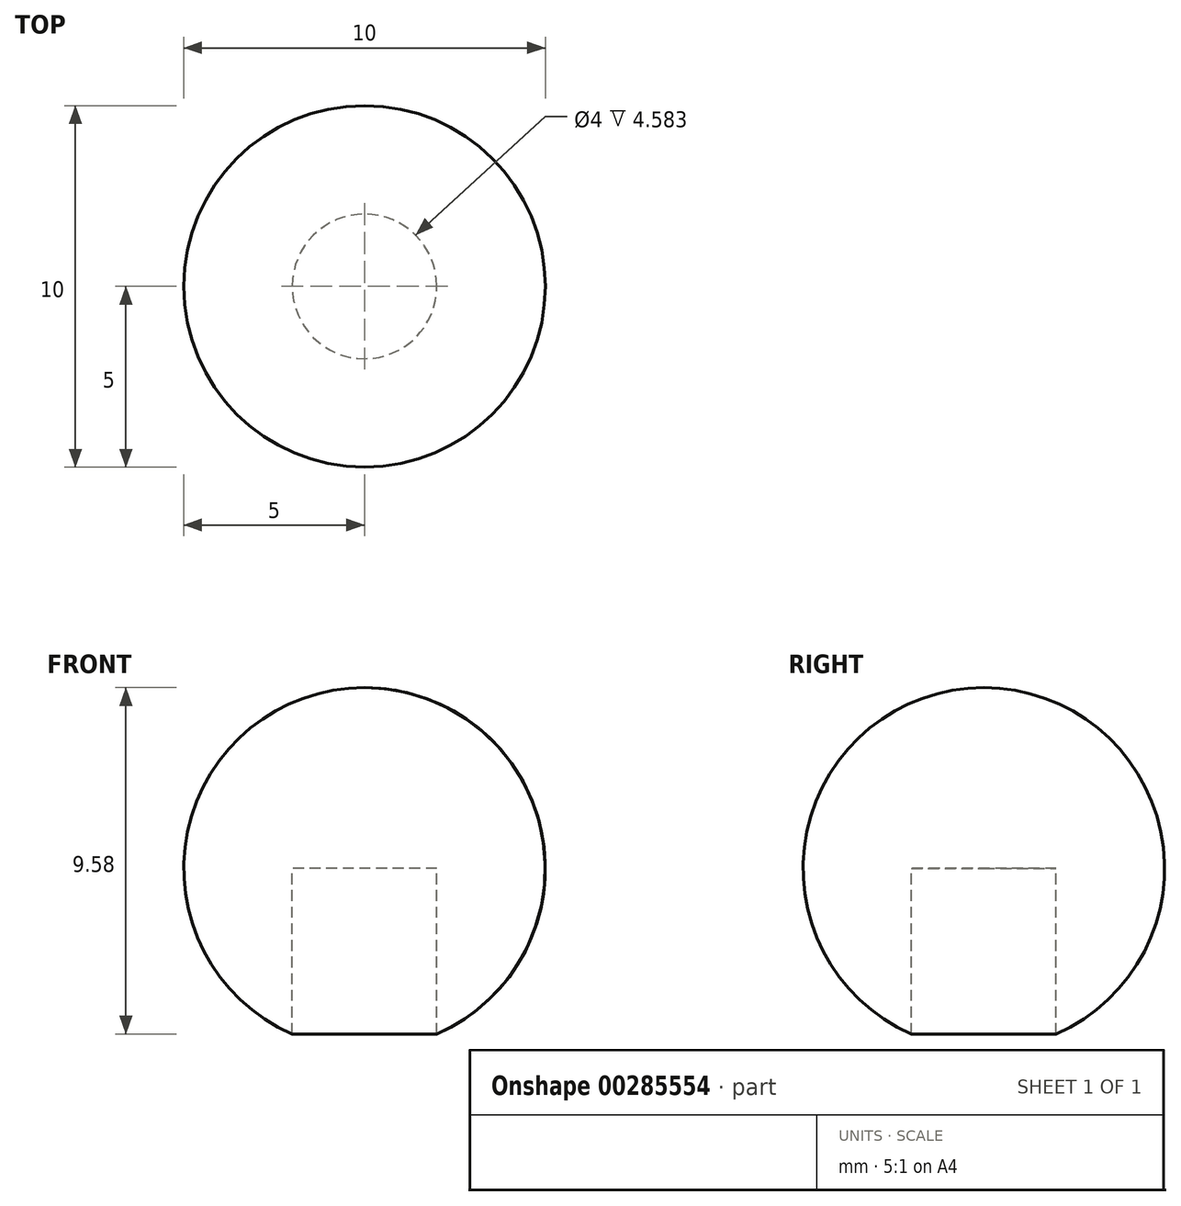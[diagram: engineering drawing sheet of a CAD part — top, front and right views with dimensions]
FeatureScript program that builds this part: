
annotation { "Feature Type Name" : "Feature", "Feature Type Description" : "" }
export const myFeature = defineFeature(function(context is Context, id is Id, definition is map)
    precondition{}
    {
        {
            var Q0;
            Q0=qCreatedBy(makeId("Front.planeOp"),FACE);
            var sketch = newSketch(context, id + "F0", { "sketchPlane" : qUnion([Q0])});
            skArc(sketch, "E0", {"start": v(0, 5) * mm, "mid": v(-5, 0) * mm, "end": v(0, -5) * mm});
            skLineSegment(sketch, "E1", {"start": v(0, 5) * mm, "end": v(0, -5) * mm});
            skSolve(sketch);
        }
        {
            var Q0;
            Q0=makeQuery(id+"F0.imprint","IMPRINT",FACE,{"disambiguationData":[TD([[makeQuery(id+"F0.imprint","IMPRINT",EDGE,{"derivedFrom":sQuery(id+"F0.wireOp",EDGE,"E0")}),1.0]])]});
            var Q1;
            Q1=sQuery(id+"F0.wireOp",EDGE,"E1");
            revolve(context, id + "F1", {"entities" : qUnion([Q0]), "axis" : qUnion([Q1]), "revolveType" : RevolveType.FULL});
        }
        {
            var Q0;
            Q0=qCreatedBy(makeId("Top.planeOp"),FACE);
            var sketch = newSketch(context, id + "F2", { "sketchPlane" : qUnion([Q0])});
            skCircle(sketch, "E2", {"center": v(0, 0) * mm, "radius": 2 * mm});
            skSolve(sketch);
        }
        {
            var Q0;
            Q0 = qSketchRegion(id + "F2", true);
            extrude(context, id + "F3", {"entities" : qUnion([Q0]), "operationType" : NewBodyOperationType.REMOVE, "oppositeDirection" : true, "depth" : 25 * mm});
        }
    });
